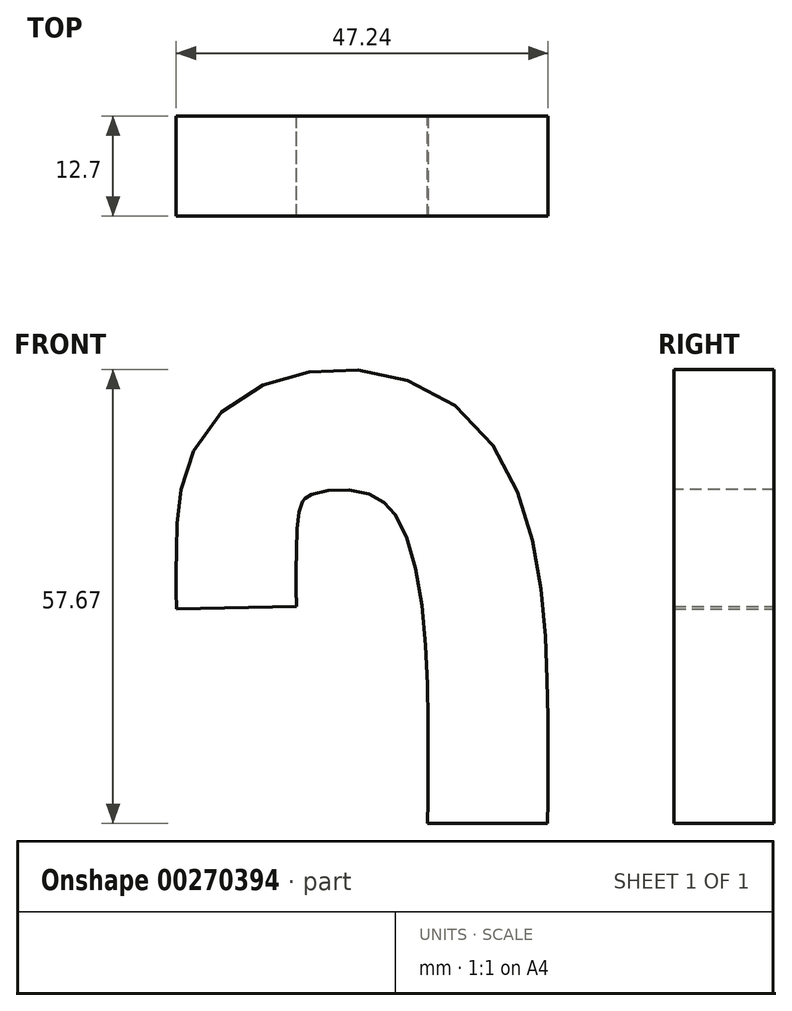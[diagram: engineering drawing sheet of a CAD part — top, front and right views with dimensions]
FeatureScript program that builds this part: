
annotation { "Feature Type Name" : "Feature", "Feature Type Description" : "" }
export const myFeature = defineFeature(function(context is Context, id is Id, definition is map)
    precondition{}
    {
        {
            var Q0;
            Q0=qCreatedBy(makeId("Top.planeOp"),FACE);
            var sketch = newSketch(context, id + "F0", { "sketchPlane" : qUnion([Q0])});
            skLineSegment(sketch, "E0.bottom", {"start": v(7.62, -6.35) * mm, "end": v(-7.62, -6.35) * mm});
            skLineSegment(sketch, "E0.top", {"start": v(7.62, 6.35) * mm, "end": v(-7.62, 6.35) * mm});
            skLineSegment(sketch, "E0.left", {"start": v(7.62, -6.35) * mm, "end": v(7.62, 6.35) * mm});
            skLineSegment(sketch, "E0.right", {"start": v(-7.62, -6.35) * mm, "end": v(-7.62, 6.35) * mm});
            skPoint(sketch, "E0.middle", {"position": v(0, 0) * mm});
            skSolve(sketch);
        }
        {
            var Q0;
            Q0=qCreatedBy(makeId("Front.planeOp"),FACE);
            var sketch = newSketch(context, id + "F1", { "sketchPlane" : qUnion([Q0])});
            skFitSpline(sketch, "E1", {"points": [v(0, 0) * mm, v(0, 14.78) * mm, v(-7.88, 46.31) * mm, v(-28.18, 47.1) * mm, v(-31.93, 35.08) * mm, v(-31.93, 27.4) * mm], "startDerivative": vector(0.76, 65.02) * mm, "endDerivative": vector(0.42, -51.1) * mm});
            skSolve(sketch);
        }
        {
            var Q0;
            Q0=makeQuery(id+"F0.imprint","IMPRINT",FACE,{"disambiguationData":[TD([[makeQuery(id+"F0.imprint","IMPRINT",EDGE,{"derivedFrom":sQuery(id+"F0.wireOp",EDGE,"E0.bottom")}),-1.0]])]});
            var Q1;
            Q1=sQuery(id+"F1.wireOp",EDGE,"E1");
            sweep(context, id + "F2", {"profiles" : qUnion([Q0]), "path" : qUnion([Q1])});
        }
    });
